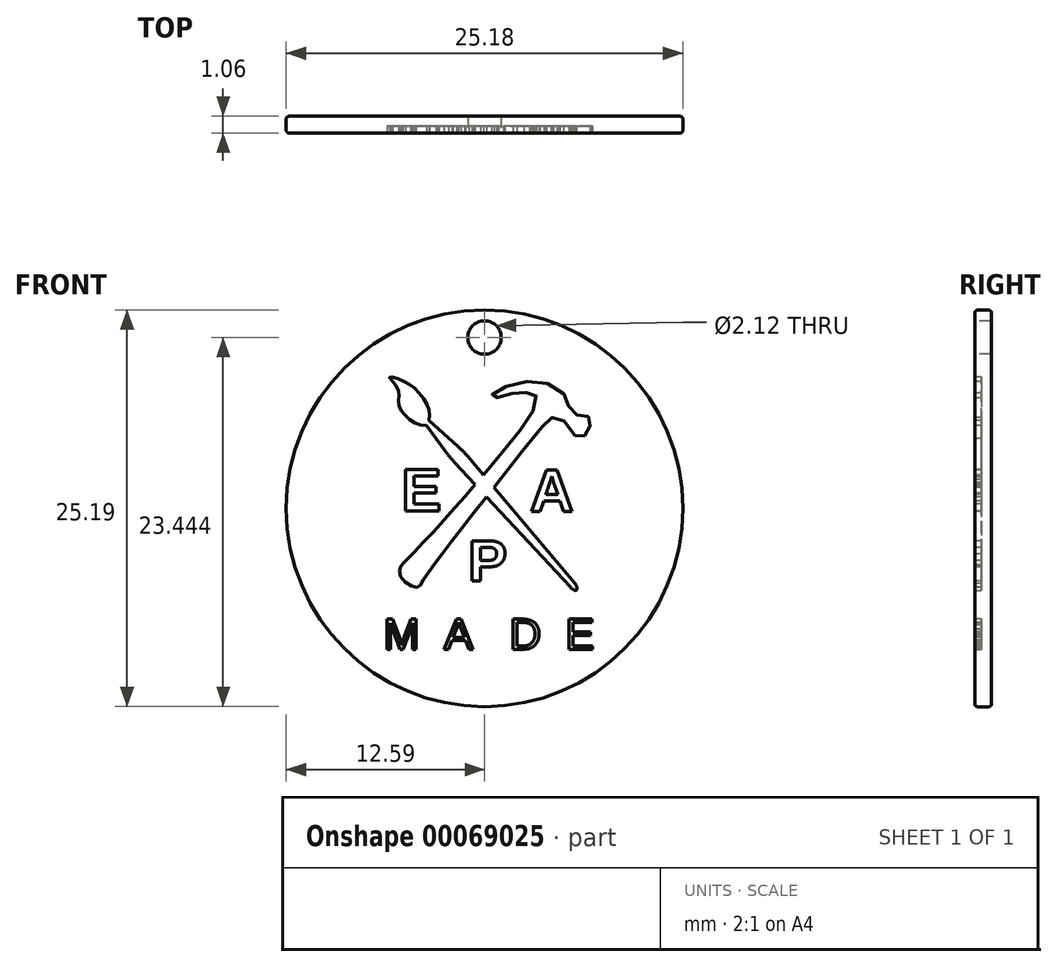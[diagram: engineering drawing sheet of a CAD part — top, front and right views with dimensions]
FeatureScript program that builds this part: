
annotation { "Feature Type Name" : "Feature", "Feature Type Description" : "" }
export const myFeature = defineFeature(function(context is Context, id is Id, definition is map)
    precondition{}
    {
        {
            var Q0;
            Q0=qCreatedBy(makeId("Front.planeOp"),FACE);
            var sketch = newSketch(context, id + "F0", { "sketchPlane" : qUnion([Q0])});
            skCircle(sketch, "E0", {"center": v(0, -4.2) * mm, "radius": 37.78 * mm});
            skSolve(sketch);
        }
        {
            var Q0;
            Q0=qCreatedBy(makeId("Front.planeOp"),FACE);
            var sketch = newSketch(context, id + "F1", { "sketchPlane" : qUnion([Q0])});
            skFitSpline(sketch, "E1", {"points": [v(9.42, 14.8) * mm, v(4.6, 7.97) * mm, v(-4.24, -2.51) * mm, v(-14.73, -13.87) * mm, v(-16.07, -15.4) * mm, v(-15.88, -17.33) * mm, v(-12.94, -19.23) * mm, v(-11.72, -18) * mm, v(-4.55, -8.27) * mm, v(10.67, 11.05) * mm, v(12.79, 13.07) * mm, v(14.9, 12.69) * mm, v(17.5, 9.51) * mm, v(18.78, 9.4) * mm, v(19.75, 10.6) * mm, v(20.23, 12.51) * mm, v(19.61, 13.39) * mm, v(17.64, 13.62) * mm, v(16.13, 15) * mm, v(15.6, 16.98) * mm, v(11.5, 19.73) * mm, v(5.44, 19.47) * mm, v(1.53, 17.62) * mm, v(1.48, 17.15) * mm, v(2.29, 16.91) * mm, v(5.35, 17.7) * mm, v(7.9, 17.85) * mm, v(9.71, 17.47) * mm, v(9.42, 14.8) * mm]});
            skSolve(sketch);
        }
        {
            var Q0;
            Q0=qSketchRegion(id+"F0",true);
            extrude(context, id + "F2", {"entities" : qUnion([Q0]), "oppositeDirection" : true, "depth" : 3.17 * mm});
        }
        {
            var Q0;
            Q0=qSketchRegion(id+"F1",true);
            extrude(context, id + "F3", {"entities" : qUnion([Q0]), "operationType" : NewBodyOperationType.REMOVE, "oppositeDirection" : true, "depth" : 1.27 * mm});
        }
        {
            var Q0;
            Q0=qCreatedBy(makeId("Front.planeOp"),FACE);
            var sketch = newSketch(context, id + "F4", { "sketchPlane" : qUnion([Q0])});
            skLineSegment(sketch, "E2", {"start": v(-10.54, 12.6) * mm, "end": v(-5.08, 7.64) * mm});
            skLineSegment(sketch, "E3", {"start": v(-2.77, 5.24) * mm, "end": v(17.27, -18.47) * mm});
            skLineSegment(sketch, "E4", {"start": v(16.34, -19.18) * mm, "end": v(-5.67, 4.55) * mm});
            skLineSegment(sketch, "E5", {"start": v(-7.42, 6.64) * mm, "end": v(-11.09, 11.57) * mm});
            skPoint(sketch, "E6.visualSharp", {"position": v(-3.85, 6.52) * mm});
            skArc(sketch, "E6.filletArc", {"start": v(-2.77, 5.24) * mm, "mid": v(-3.89, 6.48) * mm, "end": v(-5.08, 7.64) * mm});
            skPoint(sketch, "E7.visualSharp", {"position": v(-6.6, 5.55) * mm});
            skArc(sketch, "E7.filletArc", {"start": v(-7.42, 6.64) * mm, "mid": v(-6.57, 5.57) * mm, "end": v(-5.67, 4.55) * mm});
            skFitSpline(sketch, "E8", {"points": [v(-10.54, 12.6) * mm, v(-10.54, 14.33) * mm, v(-11.4, 16.34) * mm, v(-13.32, 18.7) * mm, v(-15.33, 20) * mm, v(-17.66, 20.86) * mm, v(-18.11, 20.77) * mm, v(-17.84, 20.36) * mm, v(-16.45, 18.34) * mm, v(-16.31, 16.88) * mm, v(-16.27, 15.35) * mm, v(-15.2, 13.6) * mm, v(-13.2, 12.02) * mm, v(-11.09, 11.57) * mm], "startDerivative": vector(2.69, 23.7) * mm, "endDerivative": vector(25.97, -2.9) * mm});
            skFitSpline(sketch, "E9", {"points": [v(17.27, -18.47) * mm, v(17.6, -19.27) * mm, v(17.5, -19.78) * mm, v(16.76, -19.6) * mm, v(16.34, -19.18) * mm], "startDerivative": vector(1.32, -2.83) * mm, "endDerivative": vector(-1.34, 1.87) * mm});
            skSolve(sketch);
        }
        {
            var Q0;
            Q0=qSketchRegion(id+"F4",true);
            extrude(context, id + "F5", {"entities" : qUnion([Q0]), "operationType" : NewBodyOperationType.REMOVE, "oppositeDirection" : true, "depth" : 1.27 * mm});
        }
        {
            var Q0;
            Q0=makeQuery(id+"F2.opExtrude","CAP_FACE",FACE,{"disambiguationData":[OSD([sQuery(id+"F0.wireOp",EDGE,"E0")])],"isStart":true});
            var sketch = newSketch(context, id + "F6", { "sketchPlane" : qUnion([Q0])});
            skText(sketch, "E10", { "text": "A", "fontName": "Arimo-Bold.ttf"});
            skText(sketch, "E11", { "text": "P", "fontName": "Arimo-Bold.ttf"});
            skText(sketch, "E12", { "text": "E", "fontName": "Arimo-Bold.ttf"});
            const initialGuessF6  = {"E10": [0.00864, -0.00482, 1, 0, 0.00835], "E11": [-0.0031, -0.018, 1, 0, 0.00798], "E12": [-0.01586, -0.00464, 1, 0, 0.00827]};
            skSetInitialGuess(sketch, initialGuessF6);
            skSolve(sketch);
        }
        {
            var Q0;
            Q0=qSketchRegion(id+"F6",true);
            extrude(context, id + "F7", {"entities" : qUnion([Q0]), "operationType" : NewBodyOperationType.REMOVE, "oppositeDirection" : true, "depth" : 1.27 * mm});
        }
        {
            var Q0;
            {var subQ1=sQuery(id+"F0.wireOp",EDGE,"E0");Q0=makeQuery(id+"F7.boolean.opBoolean","SPLIT",FACE,{"disambiguationData":[TD([makeQuery(id+"F2.opExtrude","SWEPT_FACE",FACE,{"disambiguationData":[OSD([subQ1])]})])],"derivedFrom":makeQuery(id+"F2.opExtrude","CAP_FACE",FACE,{"disambiguationData":[OSD([subQ1])],"isStart":true})});}
            var sketch = newSketch(context, id + "F8", { "sketchPlane" : qUnion([Q0])});
            skText(sketch, "E13", { "text": "M  A   D  E", "fontName": "Arimo-Regular.ttf"});
            const initialGuessF8  = {"E13": [-0.01926, -0.03102, 1, 0, 0.00599]};
            skSetInitialGuess(sketch, initialGuessF8);
            skSolve(sketch);
        }
        {
            var Q0;
            Q0=qSketchRegion(id+"F8",true);
            extrude(context, id + "F9", {"entities" : qUnion([Q0]), "operationType" : NewBodyOperationType.REMOVE, "oppositeDirection" : true, "depth" : 1.27 * mm});
        }
        {
            var Q0;
            {var subQ31=sQuery(id+"F0.wireOp",EDGE,"E0");var subQ32=makeQuery(id+"F2.opExtrude","SWEPT_FACE",FACE,{"disambiguationData":[OSD([subQ31])]});Q0=makeQuery(id+"F9.boolean.opBoolean","SPLIT",FACE,{"disambiguationData":[TD([subQ32])],"derivedFrom":makeQuery(id+"F7.boolean.opBoolean","SPLIT",FACE,{"disambiguationData":[TD([subQ32])],"derivedFrom":makeQuery(id+"F2.opExtrude","CAP_FACE",FACE,{"disambiguationData":[OSD([subQ31])],"isStart":true})})});}
            var sketch = newSketch(context, id + "F10", { "sketchPlane" : qUnion([Q0])});
            skCircle(sketch, "E14", {"center": v(0, 28.36) * mm, "radius": 3.17 * mm});
            skSolve(sketch);
        }
        {
            var Q0;
            Q0=qSketchRegion(id+"F10",true);
            extrude(context, id + "F11", {"entities" : qUnion([Q0]), "operationType" : NewBodyOperationType.REMOVE, "endBound" : BoundingType.THROUGH_ALL, "oppositeDirection" : true, "depth" : 25.4 * mm});
        }
        {
            var Q0;
            Q0=makeQuery(id+"F2.opExtrude","CAP_EDGE",EDGE,{"disambiguationData":[OSD([sQuery(id+"F0.wireOp",EDGE,"E0")])],"isStart":true});
            var Q1;
            Q1=makeQuery(id+"F2.opExtrude","CAP_EDGE",EDGE,{"disambiguationData":[OSD([sQuery(id+"F0.wireOp",EDGE,"E0")])],"isStart":false});
            fillet(context, id + "F12", {"entities" : qUnion([Q0, Q1]), "radius" : 0.5 * mm, "tangentPropagation" : true, "allowEdgeOverflow" : false});
        }
        {
            var Q0;
            Q0=makeQuery(id+"F7.boolean.opBoolean","SPLIT",BODY,{"disambiguationData":[OD(1.0)],"derivedFrom":makeQuery(id+"F2.opExtrude","SWEPT_BODY",BODY,{"disambiguationData":[OSD([sQuery(id+"F0.wireOp",EDGE,"E0")])]})});
            var Q1;
            Q1=makeQuery(id+"F7.boolean.opBoolean","SPLIT",BODY,{"disambiguationData":[OD(2.0)],"derivedFrom":makeQuery(id+"F2.opExtrude","SWEPT_BODY",BODY,{"disambiguationData":[OSD([sQuery(id+"F0.wireOp",EDGE,"E0")])]})});
            var Q2;
            Q2=makeQuery(id+"F9.boolean.opBoolean","SPLIT",BODY,{"disambiguationData":[OD(0.0)],"derivedFrom":makeQuery(id+"F7.boolean.opBoolean","SPLIT",BODY,{"disambiguationData":[OD(0.0)],"derivedFrom":makeQuery(id+"F2.opExtrude","SWEPT_BODY",BODY,{"disambiguationData":[OSD([sQuery(id+"F0.wireOp",EDGE,"E0")])]})})});
            var Q3;
            Q3=makeQuery(id+"F9.boolean.opBoolean","SPLIT",BODY,{"disambiguationData":[OD(1.0)],"derivedFrom":makeQuery(id+"F7.boolean.opBoolean","SPLIT",BODY,{"disambiguationData":[OD(0.0)],"derivedFrom":makeQuery(id+"F2.opExtrude","SWEPT_BODY",BODY,{"disambiguationData":[OSD([sQuery(id+"F0.wireOp",EDGE,"E0")])]})})});
            var Q4;
            Q4=makeQuery(id+"F9.boolean.opBoolean","SPLIT",BODY,{"disambiguationData":[OD(2.0)],"derivedFrom":makeQuery(id+"F7.boolean.opBoolean","SPLIT",BODY,{"disambiguationData":[OD(0.0)],"derivedFrom":makeQuery(id+"F2.opExtrude","SWEPT_BODY",BODY,{"disambiguationData":[OSD([sQuery(id+"F0.wireOp",EDGE,"E0")])]})})});
            var Q5;
            Q5=qCreatedBy(makeId("Origin.pointOp"),VERTEX);
            transform(context, id + "F13", {"entities" : qUnion([Q0, Q1, Q2, Q3, Q4]), "transformType" : TransformType.SCALE_UNIFORMLY, "scale" : 1 / 3, "scalePoint" : qUnion([Q5]), "makeCopy" : false});
        }
    });
